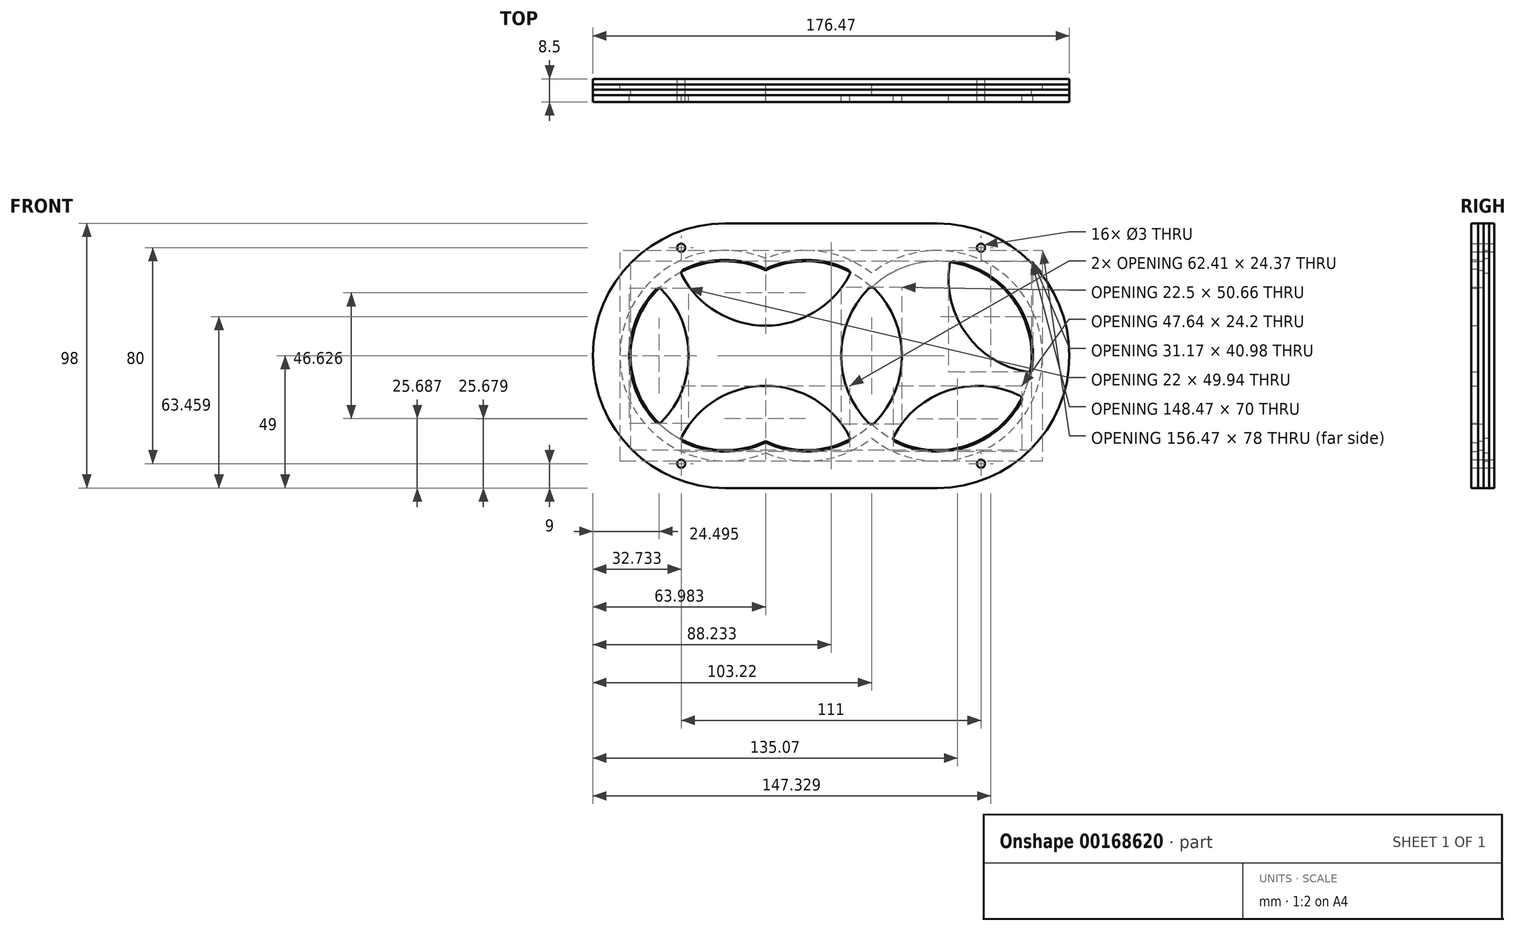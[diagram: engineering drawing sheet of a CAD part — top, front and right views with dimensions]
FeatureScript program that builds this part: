
annotation { "Feature Type Name" : "Feature", "Feature Type Description" : "" }
export const myFeature = defineFeature(function(context is Context, id is Id, definition is map)
    precondition{}
    {
        {
            var Q0;
            Q0=qCreatedBy(makeId("Front.planeOp"),FACE);
            var sketch = newSketch(context, id + "F0", { "sketchPlane" : qUnion([Q0])});
            skCircle(sketch, "E0", {"center": v(0, 0) * mm, "radius": 35 * mm});
            skLineSegment(sketch, "E1", {"start": v(0, 0) * mm, "end": v(48.5, 0) * mm});
            skCircle(sketch, "E2", {"center": v(48.5, 0) * mm, "radius": 35 * mm});
            skCircle(sketch, "E3.3.0", {"center": v(-14.99, 46.13) * mm, "radius": 35 * mm});
            skCircle(sketch, "E3.4.0", {"center": v(-39.24, 28.5) * mm, "radius": 35 * mm});
            skCircle(sketch, "E3.7.0", {"center": v(-14.99, -46.13) * mm, "radius": 35 * mm});
            skLineSegment(sketch, "E4", {"start": v(-34.45, -6.16) * mm, "end": v(-4.78, 34.67) * mm, "construction": true});
            skCircle(sketch, "E5.MirrorC", {"center": v(9.26, 28.5) * mm, "radius": 35 * mm});
            skLineSegment(sketch, "E6", {"start": v(0, 0) * mm, "end": v(9.26, 28.5) * mm});
            skLineSegment(sketch, "E7", {"start": v(0, 0) * mm, "end": v(-19.62, 14.25) * mm, "construction": true});
            skLineSegment(sketch, "E8", {"start": v(0, 0) * mm, "end": v(-29.97, 0) * mm, "construction": true});
            skCircle(sketch, "E9", {"center": v(-29.97, 0) * mm, "radius": 35 * mm});
            skLineSegment(sketch, "E10", {"start": v(24.25, 25.24) * mm, "end": v(24.25, -25.24) * mm, "construction": true});
            skCircle(sketch, "E11.MirrorC", {"center": v(63.49, -46.13) * mm, "radius": 35 * mm});
            skCircle(sketch, "E12.MirrorC", {"center": v(87.74, 28.5) * mm, "radius": 35 * mm});
            skLineSegment(sketch, "E13", {"start": v(-14.99, 31.63) * mm, "end": v(-14.99, -31.63) * mm, "construction": true});
            skCircle(sketch, "E14.MirrorC", {"center": v(-78.47, 0) * mm, "radius": 35 * mm});
            skSolve(sketch);
        }
        {
            var Q0;
            Q0=qCreatedBy(makeId("Front.planeOp"),FACE);
            var sketch = newSketch(context, id + "F1", { "sketchPlane" : qUnion([Q0])});
            skArc(sketch, "E15.0", {"start": v(24.25, -25.24) * mm, "mid": v(83.5, 0) * mm, "end": v(24.25, 25.24) * mm});
            skArc(sketch, "E16.0", {"start": v(-14.99, -31.63) * mm, "mid": v(5.63, -34.54) * mm, "end": v(24.25, -25.24) * mm});
            skArc(sketch, "E17.0", {"start": v(-14.99, 31.63) * mm, "mid": v(-64.97, 0) * mm, "end": v(-14.99, -31.63) * mm});
            skLineSegment(sketch, "E18", {"start": v(-88.68, -90.11) * mm, "end": v(-2.5, -90.11) * mm, "construction": true});
            skLineSegment(sketch, "E19.bottom", {"start": v(-29.97, 49) * mm, "end": v(48.5, 49) * mm});
            skLineSegment(sketch, "E19.top", {"start": v(-29.97, -49) * mm, "end": v(48.5, -49) * mm});
            skLineSegment(sketch, "E19.left", {"start": v(-29.97, 49) * mm, "end": v(-29.97, -49) * mm, "construction": true});
            skLineSegment(sketch, "E19.right", {"start": v(48.5, 49) * mm, "end": v(48.5, -49) * mm, "construction": true});
            skArc(sketch, "E20", {"start": v(48.5, 49) * mm, "mid": v(97.5, 0) * mm, "end": v(48.5, -49) * mm});
            skLineSegment(sketch, "E21", {"start": v(9.26, 49) * mm, "end": v(9.26, -49) * mm, "construction": true});
            skArc(sketch, "E22.MirrorCS", {"start": v(-29.97, 49) * mm, "mid": v(-78.97, 0) * mm, "end": v(-29.97, -49) * mm});
            skLineSegment(sketch, "E23", {"start": v(0, 0) * mm, "end": v(9.26, 0) * mm});
            skLineSegment(sketch, "E24.bottom", {"start": v(64.76, 40) * mm, "end": v(-46.24, 40) * mm, "construction": true});
            skLineSegment(sketch, "E24.top", {"start": v(64.76, -40) * mm, "end": v(-46.24, -40) * mm, "construction": true});
            skLineSegment(sketch, "E24.left", {"start": v(64.76, 40) * mm, "end": v(64.76, -40) * mm, "construction": true});
            skLineSegment(sketch, "E24.right", {"start": v(-46.24, 40) * mm, "end": v(-46.24, -40) * mm, "construction": true});
            skPoint(sketch, "E24.middle", {"position": v(9.26, 0) * mm});
            skArc(sketch, "E25.trimOffspring", {"start": v(24.25, 25.24) * mm, "mid": v(5.63, 34.54) * mm, "end": v(-14.99, 31.63) * mm});
            skCircle(sketch, "E26", {"center": v(-46.24, 40) * mm, "radius": 1.5 * mm});
            skCircle(sketch, "E27", {"center": v(64.76, 40) * mm, "radius": 1.5 * mm});
            skCircle(sketch, "E28", {"center": v(64.76, -40) * mm, "radius": 1.5 * mm});
            skCircle(sketch, "E29", {"center": v(-46.24, -40) * mm, "radius": 1.5 * mm});
            skSolve(sketch);
        }
        {
            var Q0;
            Q0=qCreatedBy(makeId("Front.planeOp"),FACE);
            var sketch = newSketch(context, id + "F2", { "sketchPlane" : qUnion([Q0])});
            skArc(sketch, "E30.0", {"start": v(-29.97, 49) * mm, "mid": v(-78.97, 0) * mm, "end": v(-29.97, -49) * mm});
            skLineSegment(sketch, "E30.1", {"start": v(-29.97, 49) * mm, "end": v(48.5, 49) * mm});
            skArc(sketch, "E30.2", {"start": v(48.5, 49) * mm, "mid": v(97.5, 0) * mm, "end": v(48.5, -49) * mm});
            skArc(sketch, "E30.3", {"start": v(24.25, -25.24) * mm, "mid": v(83.5, 0) * mm, "end": v(24.25, 25.24) * mm});
            skArc(sketch, "E30.4", {"start": v(24.25, 25.24) * mm, "mid": v(5.63, 34.54) * mm, "end": v(-14.99, 31.63) * mm});
            skArc(sketch, "E30.5", {"start": v(-14.99, 31.63) * mm, "mid": v(-64.97, 0) * mm, "end": v(-14.99, -31.63) * mm});
            skLineSegment(sketch, "E31.0", {"start": v(-29.97, -49) * mm, "end": v(48.5, -49) * mm});
            skArc(sketch, "E32.trimOffspring", {"start": v(-14.99, -31.63) * mm, "mid": v(5.63, -34.54) * mm, "end": v(24.25, -25.24) * mm});
            skCircle(sketch, "E33.0", {"center": v(-46.24, 40) * mm, "radius": 1.5 * mm});
            skCircle(sketch, "E33.1", {"center": v(64.76, 40) * mm, "radius": 1.5 * mm});
            skCircle(sketch, "E33.2", {"center": v(64.76, -40) * mm, "radius": 1.5 * mm});
            skCircle(sketch, "E33.3", {"center": v(-46.24, -40) * mm, "radius": 1.5 * mm});
            skSolve(sketch);
        }
        {
            var Q0;
            Q0=makeQuery(id+"F2.imprint","IMPRINT",FACE,{"disambiguationData":[TD([[makeQuery(id+"F2.imprint","IMPRINT",EDGE,{"derivedFrom":sQuery(id+"F2.wireOp",EDGE,"E30.0")}),1.0]])]});
            var Q1;
            Q1=makeQuery(id+"F2.imprint","IMPRINT",FACE,{"disambiguationData":[TD([[makeQuery(id+"F2.imprint","IMPRINT",EDGE,{"derivedFrom":sQuery(id+"F2.wireOp",EDGE,"E30.3")}),1.0]])]});
            extrude(context, id + "F3", {"entities" : qUnion([Q0, Q1]), "depth" : 2 * mm});
        }
        {
            var Q0;
            Q0=makeQuery(id+"F3.opExtrude","CAP_FACE",FACE,{"disambiguationData":[OSD([sQuery(id+"F2.wireOp",EDGE,"E30.0"),sQuery(id+"F2.wireOp",EDGE,"E30.1"),sQuery(id+"F2.wireOp",EDGE,"E30.2"),sQuery(id+"F2.wireOp",EDGE,"E31.0"),sQuery(id+"F2.wireOp",EDGE,"E33.0"),sQuery(id+"F2.wireOp",EDGE,"E33.1"),sQuery(id+"F2.wireOp",EDGE,"E33.2"),sQuery(id+"F2.wireOp",EDGE,"E33.3")])],"isStart":false});
            var sketch = newSketch(context, id + "F4", { "sketchPlane" : qUnion([Q0])});
            skArc(sketch, "E34.0", {"start": v(-29.97, 49) * mm, "mid": v(-78.97, 0) * mm, "end": v(-29.97, -49) * mm});
            skLineSegment(sketch, "E34.1", {"start": v(-29.97, 49) * mm, "end": v(48.5, 49) * mm});
            skArc(sketch, "E34.2", {"start": v(48.5, 49) * mm, "mid": v(97.5, 0) * mm, "end": v(48.5, -49) * mm});
            skLineSegment(sketch, "E34.3", {"start": v(-29.97, -49) * mm, "end": v(48.5, -49) * mm});
            skCircle(sketch, "E34.4", {"center": v(64.76, -40) * mm, "radius": 1.5 * mm});
            skCircle(sketch, "E34.5", {"center": v(-46.24, -40) * mm, "radius": 1.5 * mm});
            skPoint(sketch, "E34.6", {"position": v(-46.24, 40) * mm});
            skCircle(sketch, "E34.7", {"center": v(-46.24, 40) * mm, "radius": 1.5 * mm});
            skCircle(sketch, "E34.8", {"center": v(64.76, 40) * mm, "radius": 1.5 * mm});
            skArc(sketch, "E34.9", {"start": v(24.25, -25.24) * mm, "mid": v(83.5, 0) * mm, "end": v(24.25, 25.24) * mm, "construction": true});
            skArc(sketch, "E34.10", {"start": v(24.25, 25.24) * mm, "mid": v(5.63, 34.54) * mm, "end": v(-14.99, 31.63) * mm, "construction": true});
            skArc(sketch, "E34.11", {"start": v(-14.99, 31.63) * mm, "mid": v(-64.97, 0) * mm, "end": v(-14.99, -31.63) * mm, "construction": true});
            skArc(sketch, "E34.12", {"start": v(-14.99, -31.63) * mm, "mid": v(5.63, -34.54) * mm, "end": v(24.25, -25.24) * mm, "construction": true});
            skArc(sketch, "E35.0", {"start": v(-14.99, 36) * mm, "mid": v(-68.97, 0) * mm, "end": v(-14.99, -36) * mm});
            skArc(sketch, "E35.1", {"start": v(24.25, 30.54) * mm, "mid": v(5.38, 38.63) * mm, "end": v(-14.99, 36) * mm});
            skArc(sketch, "E35.2", {"start": v(24.25, -30.54) * mm, "mid": v(87.5, 0) * mm, "end": v(24.25, 30.54) * mm});
            skArc(sketch, "E35.3", {"start": v(-14.99, -36) * mm, "mid": v(5.38, -38.63) * mm, "end": v(24.25, -30.54) * mm});
            skSolve(sketch);
        }
        {
            var Q0;
            Q0 = qSketchRegion(id + "F4", true);
            extrude(context, id + "F5", {"entities" : qUnion([Q0]), "depth" : 2 * mm});
        }
        {
            var Q0;
            Q0=makeQuery(id+"F5.opExtrude","CAP_FACE",FACE,{"disambiguationData":[OSD([sQuery(id+"F4.wireOp",EDGE,"E34.0"),sQuery(id+"F4.wireOp",EDGE,"E34.1"),sQuery(id+"F4.wireOp",EDGE,"E34.2"),sQuery(id+"F4.wireOp",EDGE,"E34.3"),sQuery(id+"F4.wireOp",EDGE,"E34.4"),sQuery(id+"F4.wireOp",EDGE,"E34.5"),sQuery(id+"F4.wireOp",EDGE,"E34.7"),sQuery(id+"F4.wireOp",EDGE,"E34.8"),sQuery(id+"F4.wireOp",EDGE,"E35.0"),sQuery(id+"F4.wireOp",EDGE,"E35.1"),sQuery(id+"F4.wireOp",EDGE,"E35.2"),sQuery(id+"F4.wireOp",EDGE,"E35.3")])],"isStart":false});
            var sketch = newSketch(context, id + "F6", { "sketchPlane" : qUnion([Q0])});
            skArc(sketch, "E36.0", {"start": v(-29.97, 49) * mm, "mid": v(-78.97, 0) * mm, "end": v(-29.97, -49) * mm});
            skLineSegment(sketch, "E36.1", {"start": v(-29.97, 49) * mm, "end": v(48.5, 49) * mm});
            skArc(sketch, "E36.2", {"start": v(48.5, 49) * mm, "mid": v(97.5, 0) * mm, "end": v(48.5, -49) * mm});
            skLineSegment(sketch, "E36.3", {"start": v(-29.97, -49) * mm, "end": v(48.5, -49) * mm});
            skArc(sketch, "E36.4", {"start": v(24.25, -25.24) * mm, "mid": v(83.5, 0) * mm, "end": v(24.25, 25.24) * mm});
            skArc(sketch, "E36.5", {"start": v(24.25, 25.24) * mm, "mid": v(5.63, 34.54) * mm, "end": v(-14.99, 31.63) * mm});
            skArc(sketch, "E36.6", {"start": v(-14.99, 31.63) * mm, "mid": v(-64.97, 0) * mm, "end": v(-14.99, -31.63) * mm});
            skArc(sketch, "E36.7", {"start": v(-14.99, -31.63) * mm, "mid": v(5.63, -34.54) * mm, "end": v(24.25, -25.24) * mm});
            skCircle(sketch, "E36.8", {"center": v(-46.24, 40) * mm, "radius": 1.5 * mm});
            skCircle(sketch, "E36.9", {"center": v(64.76, 40) * mm, "radius": 1.5 * mm});
            skCircle(sketch, "E36.10", {"center": v(64.76, -40) * mm, "radius": 1.5 * mm});
            skCircle(sketch, "E36.11", {"center": v(-46.24, -40) * mm, "radius": 1.5 * mm});
            skSolve(sketch);
        }
        {
            var Q0;
            Q0 = qSketchRegion(id + "F6", true);
            extrude(context, id + "F7", {"entities" : qUnion([Q0]), "depth" : 2 * mm});
        }
        {
            var Q0;
            Q0=makeQuery(id+"F7.opExtrude","CAP_FACE",FACE,{"disambiguationData":[OSD([sQuery(id+"F6.wireOp",EDGE,"E36.0"),sQuery(id+"F6.wireOp",EDGE,"E36.1"),sQuery(id+"F6.wireOp",EDGE,"E36.2"),sQuery(id+"F6.wireOp",EDGE,"E36.3"),sQuery(id+"F6.wireOp",EDGE,"E36.8"),sQuery(id+"F6.wireOp",EDGE,"E36.9"),sQuery(id+"F6.wireOp",EDGE,"E36.10"),sQuery(id+"F6.wireOp",EDGE,"E36.11"),sQuery(id+"F6.wireOp",EDGE,"3844c191-1f6c-4a13-988b-1711c9720289.0"),sQuery(id+"F6.wireOp",EDGE,"3844c191-1f6c-4a13-988b-1711c9720289.1"),sQuery(id+"F6.wireOp",EDGE,"3844c191-1f6c-4a13-988b-1711c9720289.2"),sQuery(id+"F6.wireOp",EDGE,"3844c191-1f6c-4a13-988b-1711c9720289.3")])],"isStart":false});
            var sketch = newSketch(context, id + "F8", { "sketchPlane" : qUnion([Q0])});
            skArc(sketch, "E37.0", {"start": v(-29.97, 49) * mm, "mid": v(-78.97, 0) * mm, "end": v(-29.97, -49) * mm});
            skLineSegment(sketch, "E37.1", {"start": v(-29.97, 49) * mm, "end": v(48.5, 49) * mm});
            skArc(sketch, "E37.2", {"start": v(48.5, 49) * mm, "mid": v(97.5, 0) * mm, "end": v(48.5, -49) * mm});
            skLineSegment(sketch, "E37.3", {"start": v(-29.97, -49) * mm, "end": v(48.5, -49) * mm});
            skCircle(sketch, "E37.4", {"center": v(-46.24, -40) * mm, "radius": 1.5 * mm});
            skCircle(sketch, "E37.5", {"center": v(-46.24, 40) * mm, "radius": 1.5 * mm});
            skCircle(sketch, "E37.6", {"center": v(64.76, 40) * mm, "radius": 1.5 * mm});
            skCircle(sketch, "E37.7", {"center": v(64.76, -40) * mm, "radius": 1.5 * mm});
            skArc(sketch, "E38.0", {"start": v(-14.99, -32.18) * mm, "mid": v(0.21, -35.5) * mm, "end": v(15.37, -32) * mm});
            skArc(sketch, "E38.1", {"start": v(-14.99, 32.18) * mm, "mid": v(-30.19, 35.5) * mm, "end": v(-45.35, 32) * mm});
            skArc(sketch, "E38.2", {"start": v(15.37, 32) * mm, "mid": v(0.21, 35.5) * mm, "end": v(-14.99, 32.18) * mm});
            skArc(sketch, "E38.3", {"start": v(33.13, -32) * mm, "mid": v(59.47, -33.76) * mm, "end": v(79.74, -16.85) * mm});
            skArc(sketch, "E39.0", {"start": v(-53.5, 24.52) * mm, "mid": v(-43.47, 0) * mm, "end": v(-53.5, -24.52) * mm});
            skArc(sketch, "E40.0", {"start": v(-46.03, 29.95) * mm, "mid": v(-14.99, 11.13) * mm, "end": v(16.05, 29.95) * mm});
            skArc(sketch, "E41.0", {"start": v(16.05, -29.95) * mm, "mid": v(-14.99, -11.13) * mm, "end": v(-46.03, -29.95) * mm});
            skArc(sketch, "E42", {"start": v(25.32, 24.88) * mm, "mid": v(35.5, 0) * mm, "end": v(25.32, -24.88) * mm});
            skArc(sketch, "E43", {"start": v(23.18, 24.88) * mm, "mid": v(13, 0) * mm, "end": v(23.18, -24.88) * mm});
            skArc(sketch, "E44.0", {"start": v(81.95, -6.01) * mm, "mid": v(59.42, 7.94) * mm, "end": v(53.12, 33.67) * mm});
            skArc(sketch, "E45.0", {"start": v(32.45, -29.95) * mm, "mid": v(52.67, -12.84) * mm, "end": v(79.1, -14.8) * mm});
            skArc(sketch, "E46.trimOffspring", {"start": v(-45.35, -32) * mm, "mid": v(-30.19, -35.5) * mm, "end": v(-14.99, -32.18) * mm});
            skArc(sketch, "E47.trimOffspring", {"start": v(-55.66, 24.5) * mm, "mid": v(-65.47, 0) * mm, "end": v(-55.66, -24.5) * mm});
            skPoint(sketch, "E48.visualSharp", {"position": v(-54.59, 25.58) * mm});
            skArc(sketch, "E48.filletArc", {"start": v(-53.5, 24.52) * mm, "mid": v(-54.58, 24.97) * mm, "end": v(-55.66, 24.5) * mm});
            skPoint(sketch, "E49.visualSharp", {"position": v(-54.59, -25.58) * mm});
            skArc(sketch, "E49.filletArc", {"start": v(-55.66, -24.5) * mm, "mid": v(-54.58, -24.97) * mm, "end": v(-53.5, -24.52) * mm});
            skPoint(sketch, "E50.visualSharp", {"position": v(-46.7, -31.31) * mm});
            skArc(sketch, "E50.filletArc", {"start": v(-46.03, -29.95) * mm, "mid": v(-46.12, -31.12) * mm, "end": v(-45.35, -32) * mm});
            skPoint(sketch, "E51.visualSharp", {"position": v(16.72, -31.31) * mm});
            skArc(sketch, "E51.filletArc", {"start": v(15.37, -32) * mm, "mid": v(16.15, -31.12) * mm, "end": v(16.05, -29.95) * mm});
            skPoint(sketch, "E52.visualSharp", {"position": v(24.25, -25.93) * mm});
            skArc(sketch, "E52.filletArc", {"start": v(23.18, -24.88) * mm, "mid": v(24.25, -25.33) * mm, "end": v(25.32, -24.88) * mm});
            skPoint(sketch, "E53.visualSharp", {"position": v(31.78, -31.31) * mm});
            skArc(sketch, "E53.filletArc", {"start": v(32.45, -29.95) * mm, "mid": v(32.35, -31.12) * mm, "end": v(33.13, -32) * mm});
            skArc(sketch, "E54.trimOffspring", {"start": v(83.68, -4.73) * mm, "mid": v(77.22, 20.87) * mm, "end": v(54.87, 34.92) * mm});
            skPoint(sketch, "E55.visualSharp", {"position": v(16.72, 31.31) * mm});
            skArc(sketch, "E55.filletArc", {"start": v(16.05, 29.95) * mm, "mid": v(16.15, 31.12) * mm, "end": v(15.37, 32) * mm});
            skPoint(sketch, "E56.visualSharp", {"position": v(-46.7, 31.31) * mm});
            skArc(sketch, "E56.filletArc", {"start": v(-45.35, 32) * mm, "mid": v(-46.12, 31.12) * mm, "end": v(-46.03, 29.95) * mm});
            skPoint(sketch, "E57.visualSharp", {"position": v(53.38, 35.16) * mm});
            skArc(sketch, "E57.filletArc", {"start": v(54.87, 34.92) * mm, "mid": v(53.73, 34.67) * mm, "end": v(53.12, 33.67) * mm});
            skPoint(sketch, "E58.visualSharp", {"position": v(83.45, -6.23) * mm});
            skArc(sketch, "E58.filletArc", {"start": v(81.95, -6.01) * mm, "mid": v(83.09, -5.74) * mm, "end": v(83.68, -4.73) * mm});
            skPoint(sketch, "E59.visualSharp", {"position": v(80.44, -15.5) * mm});
            skArc(sketch, "E59.filletArc", {"start": v(79.74, -16.85) * mm, "mid": v(79.85, -15.69) * mm, "end": v(79.1, -14.8) * mm});
            skPoint(sketch, "E60.visualSharp", {"position": v(24.25, 25.93) * mm});
            skArc(sketch, "E60.filletArc", {"start": v(25.32, 24.88) * mm, "mid": v(24.25, 25.33) * mm, "end": v(23.18, 24.88) * mm});
            skSolve(sketch);
        }
        {
            var Q0;
            Q0 = qSketchRegion(id + "F8", true);
            extrude(context, id + "F9", {"entities" : qUnion([Q0]), "depth" : 2.5 * mm});
        }
    });
